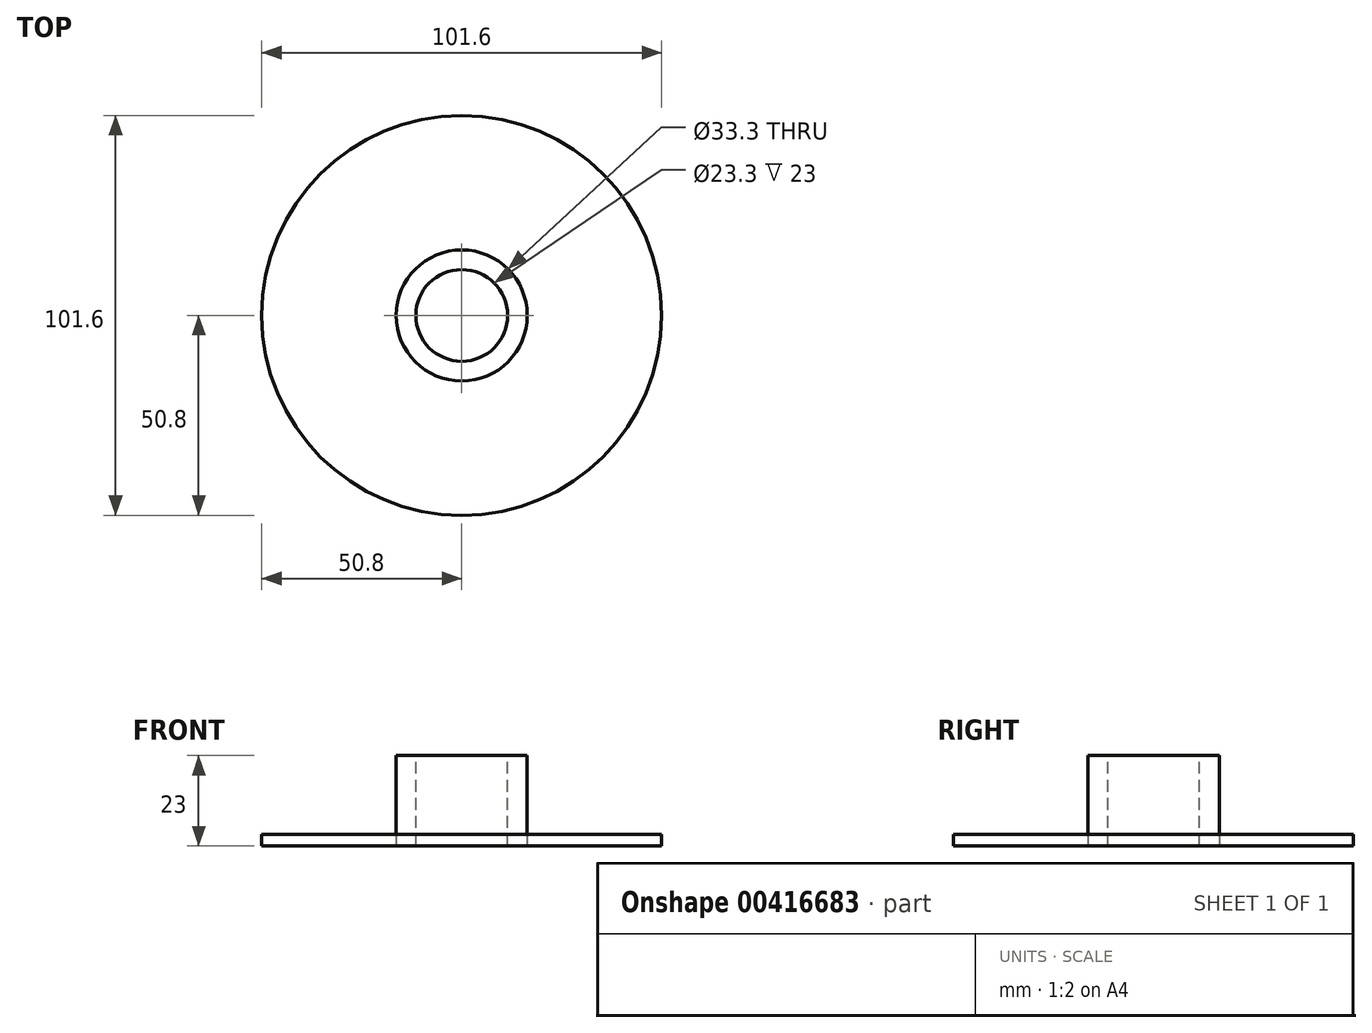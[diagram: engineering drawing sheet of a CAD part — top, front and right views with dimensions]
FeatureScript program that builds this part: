
annotation { "Feature Type Name" : "Feature", "Feature Type Description" : "" }
export const myFeature = defineFeature(function(context is Context, id is Id, definition is map)
    precondition{}
    {
        {
            var Q0;
            Q0=qCreatedBy(makeId("Top.planeOp"),FACE);
            var sketch = newSketch(context, id + "F0", { "sketchPlane" : qUnion([Q0])});
            skCircle(sketch, "E0", {"center": v(0, 0) * mm, "radius": 16.65 * mm});
            skSolve(sketch);
        }
        {
            var Q0;
            Q0=makeQuery(id+"F0.imprint","IMPRINT",FACE,{"disambiguationData":[TD([[makeQuery(id+"F0.imprint","IMPRINT",EDGE,{"derivedFrom":sQuery(id+"F0.wireOp",EDGE,"E0")}),1.0]])]});
            extrude(context, id + "F1", {"entities" : qUnion([Q0]), "depth" : 23 * mm});
        }
        {
            var Q0;
            Q0=makeQuery(id+"F1.opExtrude","CAP_FACE",FACE,{"disambiguationData":[OSD([sQuery(id+"F0.wireOp",EDGE,"E0")])],"isStart":true});
            var sketch = newSketch(context, id + "F2", { "sketchPlane" : qUnion([Q0])});
            skCircle(sketch, "E1", {"center": v(0, 0) * mm, "radius": 50.8 * mm});
            skSolve(sketch);
        }
        {
            var Q0;
            Q0=makeQuery(id+"F2.imprint","IMPRINT",FACE,{"disambiguationData":[TD([[makeQuery(id+"F2.imprint","IMPRINT",EDGE,{"derivedFrom":sQuery(id+"F2.wireOp",EDGE,"E1")}),1.0]])]});
            extrude(context, id + "F3", {"entities" : qUnion([Q0]), "oppositeDirection" : true, "depth" : 3 * mm});
        }
        {
            var Q0;
            Q0=makeQuery(id+"F1.opExtrude","CAP_FACE",FACE,{"disambiguationData":[OSD([sQuery(id+"F0.wireOp",EDGE,"E0")])],"isStart":false});
            var sketch = newSketch(context, id + "F4", { "sketchPlane" : qUnion([Q0])});
            skCircle(sketch, "E2", {"center": v(0, 0) * mm, "radius": 11.65 * mm});
            skSolve(sketch);
        }
        {
            var Q0;
            Q0=makeQuery(id+"F4.imprint","IMPRINT",FACE,{"disambiguationData":[TD([[makeQuery(id+"F4.imprint","IMPRINT",EDGE,{"derivedFrom":sQuery(id+"F4.wireOp",EDGE,"E2")}),1.0]])]});
            extrude(context, id + "F5", {"entities" : qUnion([Q0]), "operationType" : NewBodyOperationType.REMOVE, "oppositeDirection" : true, "depth" : 40 * mm});
        }
    });
